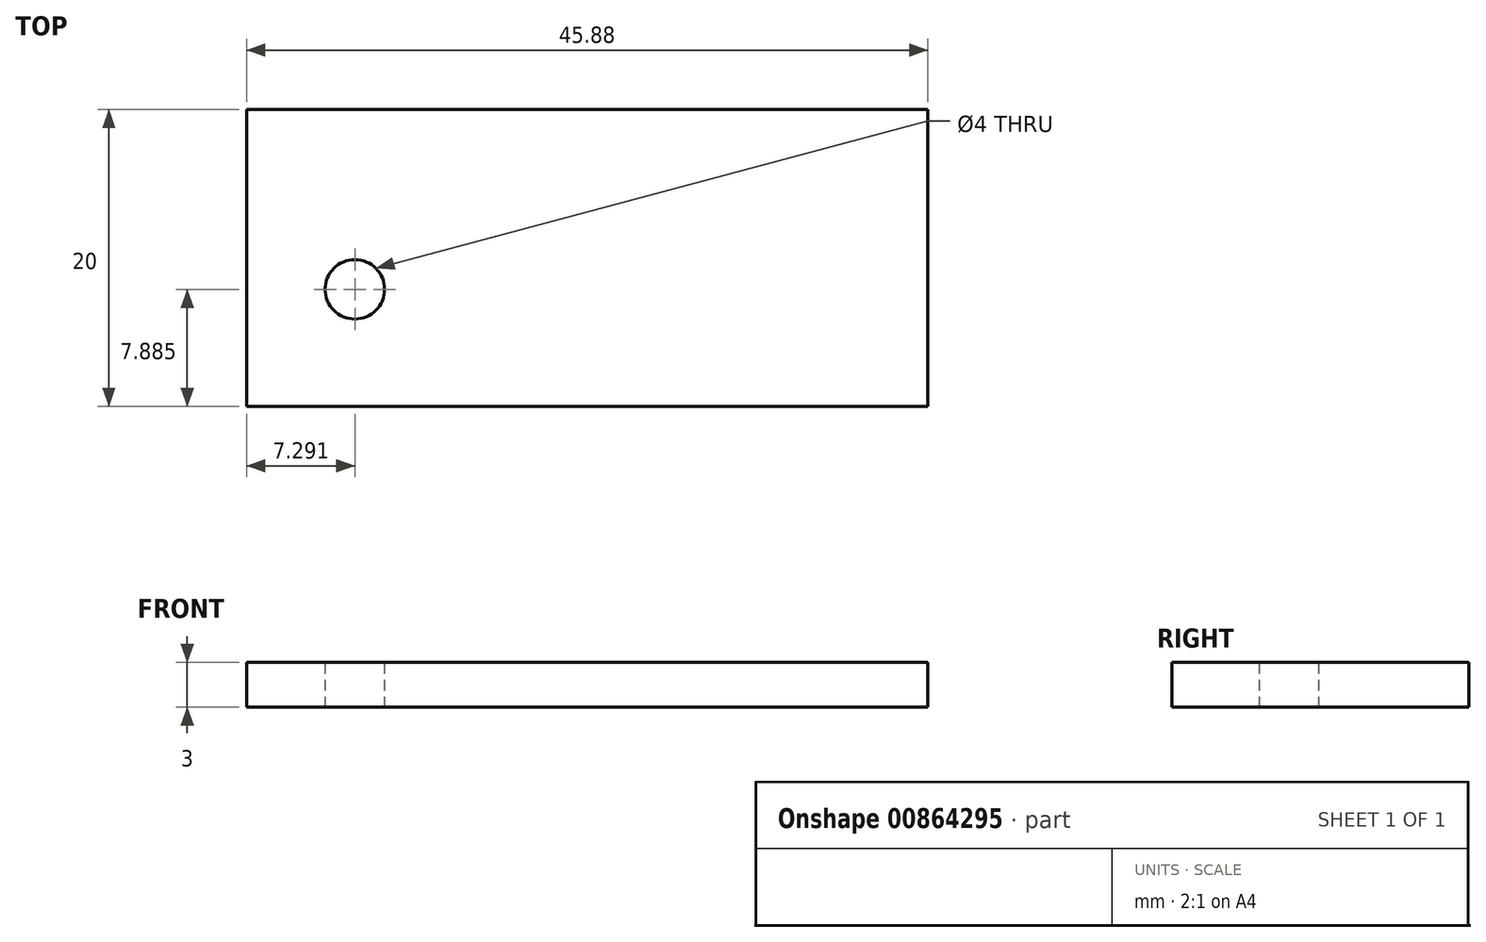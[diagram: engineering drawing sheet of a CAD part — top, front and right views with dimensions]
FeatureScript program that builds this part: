
annotation { "Feature Type Name" : "Feature", "Feature Type Description" : "" }
export const myFeature = defineFeature(function(context is Context, id is Id, definition is map)
    precondition{}
    {
        {
            var Q0;
            Q0=qCreatedBy(makeId("Top.planeOp"),FACE);
            var sketch = newSketch(context, id + "F0", { "sketchPlane" : qUnion([Q0])});
            skLineSegment(sketch, "E0.bottom", {"start": v(-22.94, 10) * mm, "end": v(22.94, 10) * mm});
            skLineSegment(sketch, "E0.top", {"start": v(-22.94, -10) * mm, "end": v(22.94, -10) * mm});
            skLineSegment(sketch, "E0.left", {"start": v(-22.94, 10) * mm, "end": v(-22.94, -10) * mm});
            skLineSegment(sketch, "E0.right", {"start": v(22.94, 10) * mm, "end": v(22.94, -10) * mm});
            skPoint(sketch, "E0.middle", {"position": v(0, 0) * mm});
            skSolve(sketch);
        }
        {
            var Q0;
            Q0=makeQuery(id+"F0.imprint","IMPRINT",FACE,{"disambiguationData":[TD([[makeQuery(id+"F0.imprint","IMPRINT",EDGE,{"derivedFrom":sQuery(id+"F0.wireOp",EDGE,"E0.bottom")}),-1.0]])]});
            extrude(context, id + "F1", {"entities" : qUnion([Q0]), "depth" : 3 * mm, "offsetDistance" : 25 * mm});
        }
        {
            var Q0;
            Q0=makeQuery(id+"F1.opExtrude","CAP_FACE",FACE,{"disambiguationData":[OSD([sQuery(id+"F0.wireOp",EDGE,"E0.bottom"),sQuery(id+"F0.wireOp",EDGE,"E0.top"),sQuery(id+"F0.wireOp",EDGE,"E0.left"),sQuery(id+"F0.wireOp",EDGE,"E0.right")])],"isStart":false});
            var sketch = newSketch(context, id + "F2", { "sketchPlane" : qUnion([Q0])});
            skCircle(sketch, "E1", {"center": v(-15.65, -2.11) * mm, "radius": 2 * mm});
            skSolve(sketch);
        }
        {
            var Q0;
            Q0 = qSketchRegion(id + "F2", true);
            extrude(context, id + "F3", {"entities" : qUnion([Q0]), "operationType" : NewBodyOperationType.REMOVE, "endBound" : BoundingType.THROUGH_ALL, "depth" : 25 * mm, "offsetDistance" : 25 * mm, "hasSecondDirection" : true, "secondDirectionOppositeDirection" : true, "secondDirectionDepth" : 25 * mm});
        }
    });
